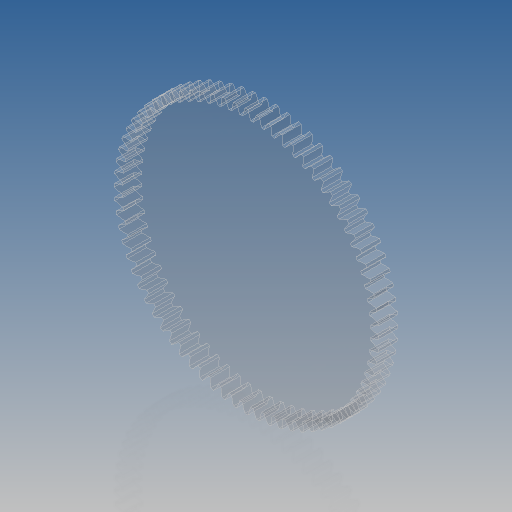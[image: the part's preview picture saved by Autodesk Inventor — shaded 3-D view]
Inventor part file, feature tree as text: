
AUTODESK INVENTOR PART (.ipt)
format: ipt  version: 2017 (Build 210142000, 142)  size: 428,032 bytes
history: native  units: mm (DEFAULTED — no unit token found)
features: plane x3, other x3, sketch x2, extrude x1
ambient origin geometry x8: Origin, YZ Plane, XZ Plane, XY Plane, X Axis, Y Axis, Z Axis, Center Point
bodies: Solid1 (feature_tree)
feature tree (9):
  extrude  "Extrusion1"  Depth=8.0mm TaperAngle=0.0deg
  plane  "Work Plane2"
  plane  "Work Plane8"
  plane  "Work Plane9"
  other  "Engranaje recto"
  sketch  "Sketch1"  dims[d0=111.0mm d1=8.0mm d2=0.0mm]
  sketch  "Sketch2"  dims[d3=108.0mm d4=10.0mm d5=0.0mm d16=67.5mm d17=0.0mm d34=0.436332mm d39=0.0mm d41=0.0mm d43=67.5mm d46=67.5mm d47=0.0mm d48=0.0mm]
  other  "Srf1"
  other  "Diámetro de separación"
